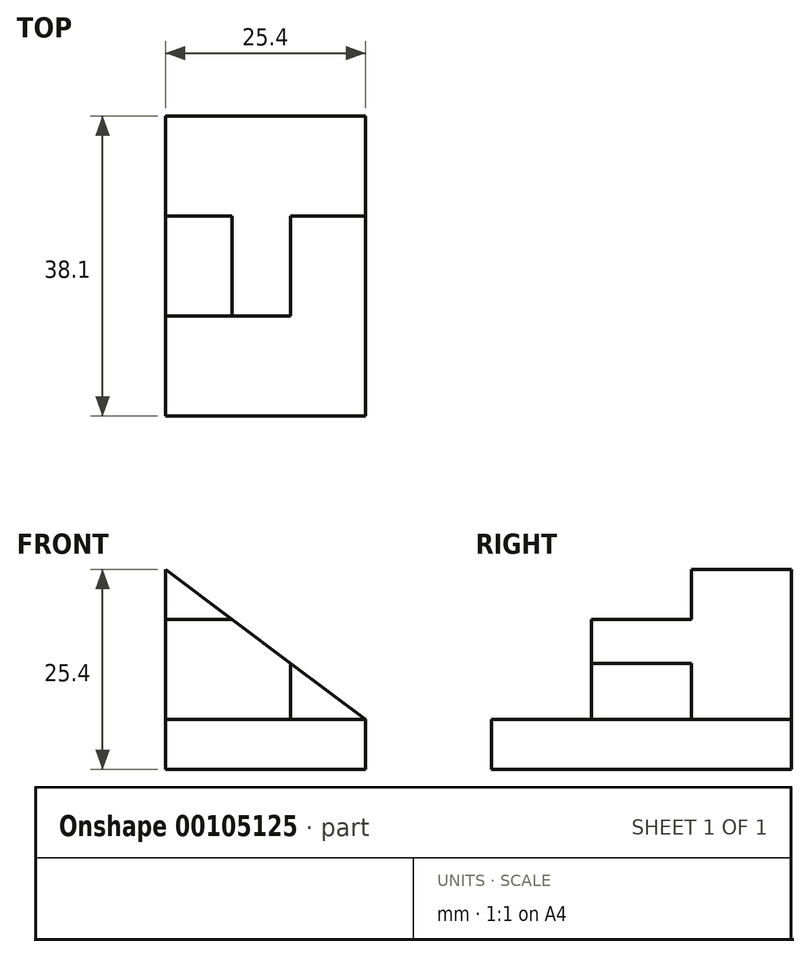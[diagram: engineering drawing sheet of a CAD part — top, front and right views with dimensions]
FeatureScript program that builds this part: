
annotation { "Feature Type Name" : "Feature", "Feature Type Description" : "" }
export const myFeature = defineFeature(function(context is Context, id is Id, definition is map)
    precondition{}
    {
        {
            var Q0;
            Q0=qCreatedBy(makeId("Front.planeOp"),FACE);
            var sketch = newSketch(context, id + "F0", { "sketchPlane" : qUnion([Q0])});
            skLineSegment(sketch, "E0", {"start": v(0, 0) * mm, "end": v(0, 25.4) * mm});
            skLineSegment(sketch, "E1", {"start": v(0, 25.4) * mm, "end": v(25.4, 25.4) * mm});
            skLineSegment(sketch, "E2", {"start": v(25.4, 25.4) * mm, "end": v(25.4, 0) * mm});
            skLineSegment(sketch, "E3", {"start": v(25.4, 0) * mm, "end": v(0, 0) * mm});
            skSolve(sketch);
        }
        {
            var Q0;
            Q0 = qSketchRegion(id + "F0", true);
            extrude(context, id + "F1", {"entities" : qUnion([Q0]), "oppositeDirection" : true, "depth" : 38.1 * mm});
        }
        {
            var Q0;
            Q0=makeQuery(id+"F1.opExtrude","CAP_FACE",FACE,{"disambiguationData":[OSD([sQuery(id+"F0.wireOp",EDGE,"E0"),sQuery(id+"F0.wireOp",EDGE,"E1"),sQuery(id+"F0.wireOp",EDGE,"E2"),sQuery(id+"F0.wireOp",EDGE,"E3")])],"isStart":true});
            var sketch = newSketch(context, id + "F2", { "sketchPlane" : qUnion([Q0])});
            skLineSegment(sketch, "E4", {"start": v(0, 25.4) * mm, "end": v(25.4, 6.35) * mm});
            skSolve(sketch);
        }
        {
            var Q0;
            {var subQ0=sQuery(id+"F2.wireOp",EDGE,"E4");Q0=makeQuery(id+"F2.imprint","IMPRINT",FACE,{"disambiguationData":[TD([[makeQuery(id+"F2.imprint","IMPRINT",EDGE,{"derivedFrom":subQ0}),1.0]])]});}
            extrude(context, id + "F3", {"entities" : qUnion([Q0]), "operationType" : NewBodyOperationType.REMOVE, "endBound" : BoundingType.THROUGH_ALL, "oppositeDirection" : true, "depth" : 25.4 * mm});
        }
        {
            var Q0;
            Q0=makeQuery(id+"F1.opExtrude","CAP_FACE",FACE,{"disambiguationData":[OSD([sQuery(id+"F0.wireOp",EDGE,"E0"),sQuery(id+"F0.wireOp",EDGE,"E1"),sQuery(id+"F0.wireOp",EDGE,"E2"),sQuery(id+"F0.wireOp",EDGE,"E3")])],"isStart":true});
            var sketch = newSketch(context, id + "F4", { "sketchPlane" : qUnion([Q0])});
            skLineSegment(sketch, "E5", {"start": v(0, 25.4) * mm, "end": v(0, 19.05) * mm});
            skLineSegment(sketch, "E6", {"start": v(0, 19.05) * mm, "end": v(8.47, 19.05) * mm});
            skSolve(sketch);
        }
        {
            var Q0;
            {var subQ0=sQuery(id+"F4.wireOp",EDGE,"E5");Q0=makeQuery(id+"F4.imprint","IMPRINT",FACE,{"disambiguationData":[TD([[makeQuery(id+"F4.imprint","IMPRINT",EDGE,{"derivedFrom":subQ0}),-1.0]])]});}
            extrude(context, id + "F5", {"entities" : qUnion([Q0]), "operationType" : NewBodyOperationType.REMOVE, "oppositeDirection" : true, "depth" : 25.4 * mm});
        }
        {
            var Q0;
            Q0=makeQuery(id+"F1.opExtrude","CAP_FACE",FACE,{"disambiguationData":[OSD([sQuery(id+"F0.wireOp",EDGE,"E0"),sQuery(id+"F0.wireOp",EDGE,"E1"),sQuery(id+"F0.wireOp",EDGE,"E2"),sQuery(id+"F0.wireOp",EDGE,"E3")])],"isStart":true});
            var sketch = newSketch(context, id + "F6", { "sketchPlane" : qUnion([Q0])});
            skLineSegment(sketch, "E7", {"start": v(0, 6.35) * mm, "end": v(25.4, 6.35) * mm});
            skSolve(sketch);
        }
        {
            var Q0;
            {var subQ0=sQuery(id+"F6.wireOp",EDGE,"E7");Q0=makeQuery(id+"F6.imprint","IMPRINT",FACE,{"disambiguationData":[TD([[makeQuery(id+"F6.imprint","IMPRINT",EDGE,{"derivedFrom":subQ0}),1.0]])]});}
            extrude(context, id + "F7", {"entities" : qUnion([Q0]), "operationType" : NewBodyOperationType.REMOVE, "oppositeDirection" : true, "depth" : 12.7 * mm});
        }
        {
            var Q0;
            Q0=makeQuery(id+"F7.boolean.opBoolean","COPY",FACE,{"derivedFrom":makeQuery(id+"F7.opExtrude","CAP_FACE",FACE,{"disambiguationData":[OSD([sQuery(id+"F0.wireOp",EDGE,"E0"),sQuery(id+"F2.wireOp",EDGE,"E4"),sQuery(id+"F4.wireOp",EDGE,"E6"),sQuery(id+"F6.wireOp",EDGE,"E7")])],"isStart":false})});
            var sketch = newSketch(context, id + "F8", { "sketchPlane" : qUnion([Q0])});
            skLineSegment(sketch, "E8", {"start": v(15.88, 13.5) * mm, "end": v(15.88, 6.35) * mm});
            skLineSegment(sketch, "E9", {"start": v(15.88, 6.35) * mm, "end": v(25.4, 6.35) * mm});
            skLineSegment(sketch, "E10", {"start": v(25.4, 6.35) * mm, "end": v(15.88, 13.5) * mm});
            skSolve(sketch);
        }
        {
            var Q0;
            Q0=makeQuery(id+"F8.imprint","IMPRINT",FACE,{"disambiguationData":[TD([[makeQuery(id+"F8.imprint","IMPRINT",EDGE,{"derivedFrom":sQuery(id+"F8.wireOp",EDGE,"E8")}),1.0]])]});
            extrude(context, id + "F9", {"entities" : qUnion([Q0]), "operationType" : NewBodyOperationType.REMOVE, "oppositeDirection" : true, "depth" : 12.7 * mm});
        }
    });
